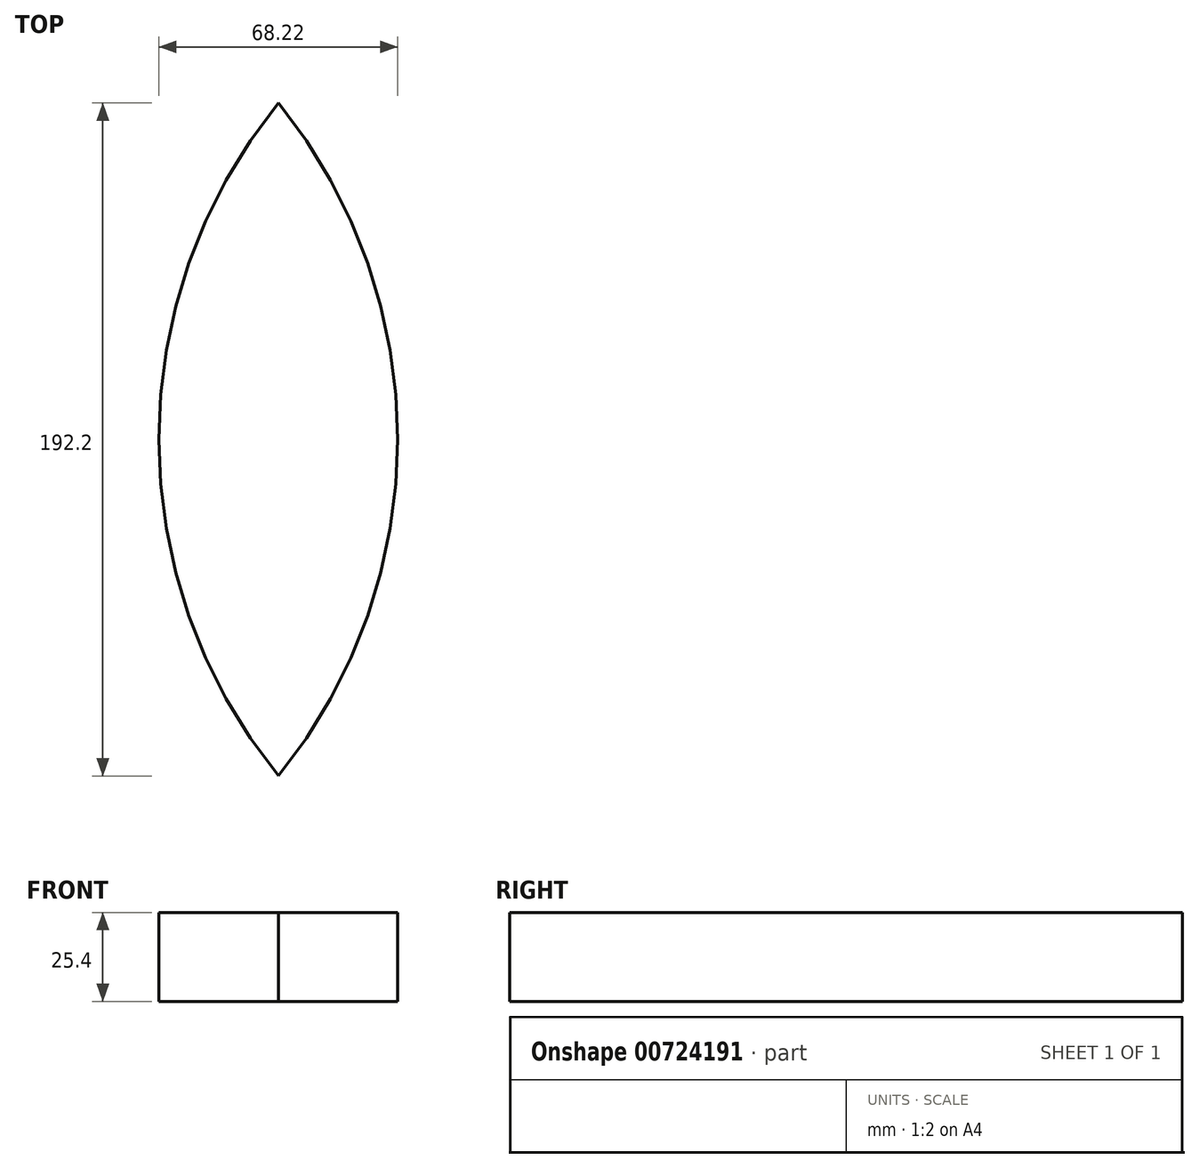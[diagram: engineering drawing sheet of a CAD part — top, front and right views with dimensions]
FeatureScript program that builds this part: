
annotation { "Feature Type Name" : "Feature", "Feature Type Description" : "" }
export const myFeature = defineFeature(function(context is Context, id is Id, definition is map)
    precondition{}
    {
        {
            var Q0;
            Q0=qCreatedBy(makeId("Top.planeOp"),FACE);
            var sketch = newSketch(context, id + "F0", { "sketchPlane" : qUnion([Q0])});
            skArc(sketch, "E0", {"start": v(0, 96.1) * mm, "mid": v(-34.11, 0) * mm, "end": v(0, -96.1) * mm});
            skArc(sketch, "E1.MirrorCS", {"start": v(0, 96.1) * mm, "mid": v(34.11, 0) * mm, "end": v(0, -96.1) * mm});
            skPoint(sketch, "E2.MirrorCS.end.orphan", {"position": v(35.15, 23.38) * mm});
            skPoint(sketch, "E2.MirrorCS.start.orphan", {"position": v(23.69, 60.94) * mm});
            skPoint(sketch, "E3.end.orphan", {"position": v(-35.15, 23.38) * mm});
            skPoint(sketch, "E4.MirrorCS.end.orphan", {"position": v(-35.15, -23.38) * mm});
            skPoint(sketch, "E4.MirrorCS.start.orphan", {"position": v(-23.69, -60.94) * mm});
            skPoint(sketch, "E5.MirrorCS.end.orphan", {"position": v(35.15, -23.38) * mm});
            skPoint(sketch, "E5.MirrorCS.start.orphan", {"position": v(23.69, -60.94) * mm});
            skPoint(sketch, "E6.end.orphan", {"position": v(-23.69, 60.94) * mm});
            skPoint(sketch, "E7.MirrorCS.end.orphan", {"position": v(16.38, 74.86) * mm});
            skPoint(sketch, "E7.MirrorCS.start.orphan", {"position": v(0, 96.1) * mm});
            skPoint(sketch, "E8.end.orphan", {"position": v(-16.38, 74.86) * mm});
            skPoint(sketch, "E9.MirrorCS.start.orphan", {"position": v(-16.38, -74.86) * mm});
            skPoint(sketch, "E10.MirrorCS.end.orphan", {"position": v(16.38, -74.86) * mm});
            skPoint(sketch, "E10.MirrorCS.start.orphan", {"position": v(0, -96.1) * mm});
            skEllipse(sketch, "E11", {"center": v(0, 18.35) * mm, "majorRadius": 18.35 * mm, "minorRadius": 18.17 * mm, "majorAxis": v(0, -1)});
            skSolve(sketch);
        }
        {
            var Q0;
            Q0 = qSketchRegion(id + "F0", true);
            var Q1;
            Q1=makeQuery(id+"F0.imprint","IMPRINT",FACE,{"disambiguationData":[TD([[makeQuery(id+"F0.imprint","IMPRINT",EDGE,{"derivedFrom":sQuery(id+"F0.wireOp",EDGE,"E11")}),1.0]])]});
            extrude(context, id + "F1", {"entities" : qUnion([Q0, Q1]), "depth" : 25.4 * mm, "offsetDistance" : 25.4 * mm});
        }
    });
